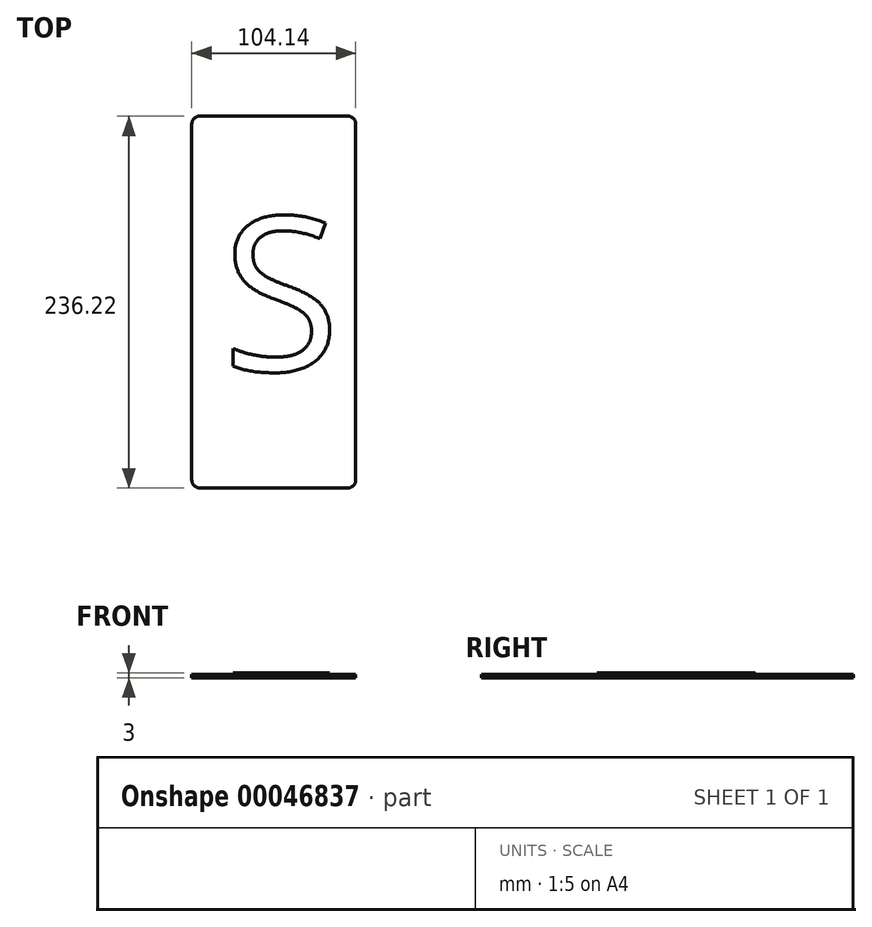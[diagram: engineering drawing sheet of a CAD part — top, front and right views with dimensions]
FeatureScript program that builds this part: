
annotation { "Feature Type Name" : "Feature", "Feature Type Description" : "" }
export const myFeature = defineFeature(function(context is Context, id is Id, definition is map)
    precondition{}
    {
        {
            var Q0;
            Q0=qCreatedBy(makeId("Top.planeOp"),FACE);
            var sketch = newSketch(context, id + "F0", { "sketchPlane" : qUnion([Q0])});
            skLineSegment(sketch, "E0.bottom", {"start": v(-50.77, 205.74) * mm, "end": v(53.37, 205.74) * mm});
            skLineSegment(sketch, "E0.top", {"start": v(-50.77, -30.48) * mm, "end": v(53.37, -30.48) * mm});
            skLineSegment(sketch, "E0.left", {"start": v(-50.77, 205.74) * mm, "end": v(-50.77, -30.48) * mm});
            skLineSegment(sketch, "E0.right", {"start": v(53.37, 205.74) * mm, "end": v(53.37, -30.48) * mm});
            skSolve(sketch);
        }
        {
            var Q0;
            Q0=makeQuery(id+"F0.imprint","IMPRINT",FACE,{"disambiguationData":[TD([[makeQuery(id+"F0.imprint","IMPRINT",EDGE,{"derivedFrom":sQuery(id+"F0.wireOp",EDGE,"E0.bottom")}),-1.0]])]});
            extrude(context, id + "F1", {"entities" : qUnion([Q0]), "depth" : 2 * mm});
        }
        {
            var Q0;
            Q0=makeQuery(id+"F1.opExtrude","CAP_FACE",FACE,{"disambiguationData":[OSD([sQuery(id+"F0.wireOp",EDGE,"E0.bottom"),sQuery(id+"F0.wireOp",EDGE,"E0.top"),sQuery(id+"F0.wireOp",EDGE,"E0.left"),sQuery(id+"F0.wireOp",EDGE,"E0.right")])],"isStart":false});
            var sketch = newSketch(context, id + "F2", { "sketchPlane" : qUnion([Q0])});
            skText(sketch, "E1", { "text": "S\n", "fontName": "OpenSans-Regular.ttf"});
            const initialGuessF2  = {"E1": [-0.03177, 0.04404, 1, 0, 0.09846]};
            skSetInitialGuess(sketch, initialGuessF2);
            skSolve(sketch);
        }
        {
            var Q0;
            Q0 = qSketchRegion(id + "F2", true);
            extrude(context, id + "F3", {"entities" : qUnion([Q0]), "operationType" : NewBodyOperationType.ADD, "depth" : 1 * mm});
        }
        {
            var Q0;
            Q0=makeQuery(id+"F1.opExtrude","SWEPT_EDGE",EDGE,{"disambiguationData":[OSD([sQuery(id+"F0.wireOp",EDGE,"E0.bottom"),sQuery(id+"F0.wireOp",EDGE,"E0.left")])]});
            var Q1;
            Q1=makeQuery(id+"F1.opExtrude","SWEPT_EDGE",EDGE,{"disambiguationData":[OSD([sQuery(id+"F0.wireOp",EDGE,"E0.bottom"),sQuery(id+"F0.wireOp",EDGE,"E0.right")])]});
            var Q2;
            Q2=makeQuery(id+"F1.opExtrude","SWEPT_EDGE",EDGE,{"disambiguationData":[OSD([sQuery(id+"F0.wireOp",EDGE,"E0.top"),sQuery(id+"F0.wireOp",EDGE,"E0.left")])]});
            var Q3;
            Q3=makeQuery(id+"F1.opExtrude","SWEPT_EDGE",EDGE,{"disambiguationData":[OSD([sQuery(id+"F0.wireOp",EDGE,"E0.top"),sQuery(id+"F0.wireOp",EDGE,"E0.right")])]});
            fillet(context, id + "F4", {"entities" : qUnion([Q0, Q1, Q2, Q3]), "radius" : 5.08 * mm, "tangentPropagation" : true, "allowEdgeOverflow" : false});
        }
    });
